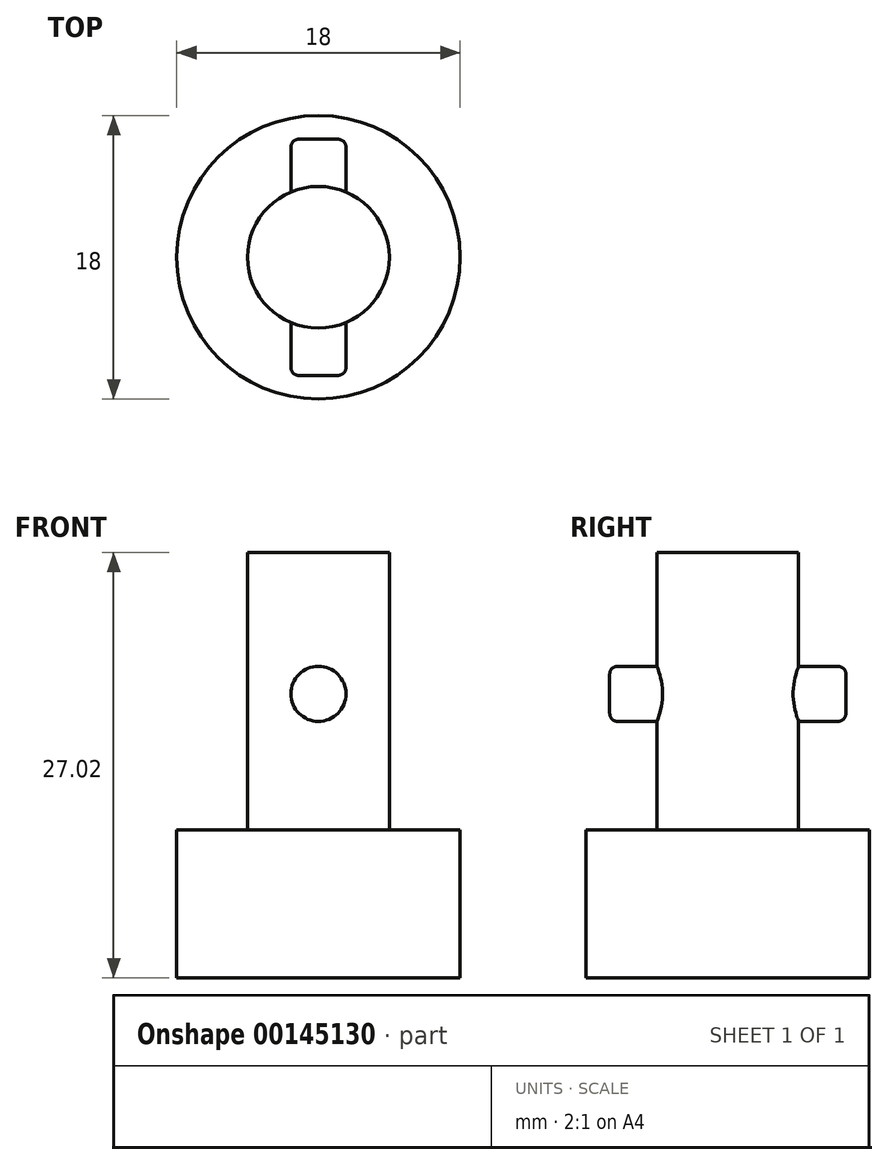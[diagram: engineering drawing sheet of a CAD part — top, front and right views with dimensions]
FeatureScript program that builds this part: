
annotation { "Feature Type Name" : "Feature", "Feature Type Description" : "" }
export const myFeature = defineFeature(function(context is Context, id is Id, definition is map)
    precondition{}
    {
        {
            var Q0;
            Q0=qCreatedBy(makeId("Top.planeOp"),FACE);
            var sketch = newSketch(context, id + "F0", { "sketchPlane" : qUnion([Q0])});
            skCircle(sketch, "E0", {"center": v(0, 0) * mm, "radius": 9 * mm});
            skSolve(sketch);
        }
        {
            var Q0;
            Q0=makeQuery(id+"F0.imprint","IMPRINT",FACE,{"disambiguationData":[TD([[makeQuery(id+"F0.imprint","IMPRINT",EDGE,{"derivedFrom":sQuery(id+"F0.wireOp",EDGE,"E0")}),1.0]])]});
            extrude(context, id + "F1", {"entities" : qUnion([Q0]), "depth" : 45 * mm});
        }
        {
            var Q0;
            Q0=makeQuery(id+"F1.opExtrude","CAP_FACE",FACE,{"disambiguationData":[OSD([sQuery(id+"F0.wireOp",EDGE,"E0")])],"isStart":false});
            var sketch = newSketch(context, id + "F2", { "sketchPlane" : qUnion([Q0])});
            skCircle(sketch, "E1", {"center": v(0, 0) * mm, "radius": 4.5 * mm});
            skSolve(sketch);
        }
        {
            var Q0;
            Q0 = qSketchRegion(id + "F2", true);
            extrude(context, id + "F3", {"entities" : qUnion([Q0]), "operationType" : NewBodyOperationType.ADD, "depth" : 25 * mm});
        }
        {
            var Q0;
            Q0=qCreatedBy(makeId("Top.planeOp"),FACE);
            var sketch = newSketch(context, id + "F4", { "sketchPlane" : qUnion([Q0])});
            skLineSegment(sketch, "E2", {"start": v(-55.26, 0) * mm, "end": v(54.36, 0) * mm});
            skSolve(sketch);
        }
        {
            var Q0;
            Q0=sQuery(id+"F4.wireOp",EDGE,"E2");
            cPlane(context, id + "F5", {"entities" : qUnion([Q0]), "cplaneType" : CPlaneType.LINE_ANGLE, "offset" : 25 * mm, "angle" : 0 * degree, "width" : 150 * mm, "height" : 150 * mm});
        }
        {
            var Q0;
            Q0=makeQuery(id+"F3.opExtrude","CAP_FACE",FACE,{"disambiguationData":[OSD([sQuery(id+"F2.wireOp",EDGE,"E1")])],"isStart":false});
            extrude(context, id + "F6", {"entities" : qUnion([Q0]), "operationType" : NewBodyOperationType.ADD, "depth" : 25 * mm});
        }
        {
            var Q0;
            Q0=qCreatedBy(id+"F5.planeOp",FACE);
            var sketch = newSketch(context, id + "F7", { "sketchPlane" : qUnion([Q0])});
            skCircle(sketch, "E3", {"center": v(0, 53.65) * mm, "radius": 1.75 * mm});
            skSolve(sketch);
        }
        {
            var Q0;
            Q0 = qSketchRegion(id + "F7", true);
            var Q1;
            Q1 = qSketchRegion(id + "F4", true);
            extrude(context, id + "F8", {"entities" : qUnion([Q0, Q1]), "operationType" : NewBodyOperationType.ADD, "depth" : 15 * mm, "symmetric" : true});
        }
        {
            var Q0;
            Q0=makeQuery(id+"F8.opExtrude","CAP_FACE",FACE,{"disambiguationData":[OSD([sQuery(id+"F7.wireOp",EDGE,"E3")])],"isStart":true});
            fillet(context, id + "F9", {"entities" : qUnion([Q0]), "radius" : .5 * mm, "tangentPropagation" : true, "allowEdgeOverflow" : false});
        }
        {
            var Q0;
            Q0=makeQuery(id+"F8.opExtrude","CAP_FACE",FACE,{"disambiguationData":[OSD([sQuery(id+"F7.wireOp",EDGE,"E3")])],"isStart":false});
            fillet(context, id + "F10", {"entities" : qUnion([Q0]), "radius" : .5 * mm, "tangentPropagation" : true, "allowEdgeOverflow" : false});
        }
        {
            var Q0;
            Q0=makeQuery(id+"F6.opExtrude","CAP_FACE",FACE,{"disambiguationData":[OSD([sQuery(id+"F2.wireOp",EDGE,"E1")])],"isStart":false});
            extrude(context, id + "F11", {"entities" : qUnion([Q0]), "operationType" : NewBodyOperationType.ADD, "oppositeDirection" : true, "depth" : 32 * mm});
        }
        {
            var Q0;
            Q0=makeQuery(id+"F6.opExtrude","CAP_FACE",FACE,{"disambiguationData":[OSD([sQuery(id+"F2.wireOp",EDGE,"E1")])],"isStart":false});
            extrude(context, id + "F12", {"entities" : qUnion([Q0]), "operationType" : NewBodyOperationType.REMOVE, "oppositeDirection" : true, "depth" : 32.37 * mm});
        }
        {
            var Q0;
            Q0=makeQuery(id+"F0.imprint","IMPRINT",FACE,{"disambiguationData":[TD([[makeQuery(id+"F0.imprint","IMPRINT",EDGE,{"derivedFrom":sQuery(id+"F0.wireOp",EDGE,"E0")}),1.0]])]});
            extrude(context, id + "F13", {"entities" : qUnion([Q0]), "operationType" : NewBodyOperationType.REMOVE, "depth" : 35.6 * mm});
        }
    });
